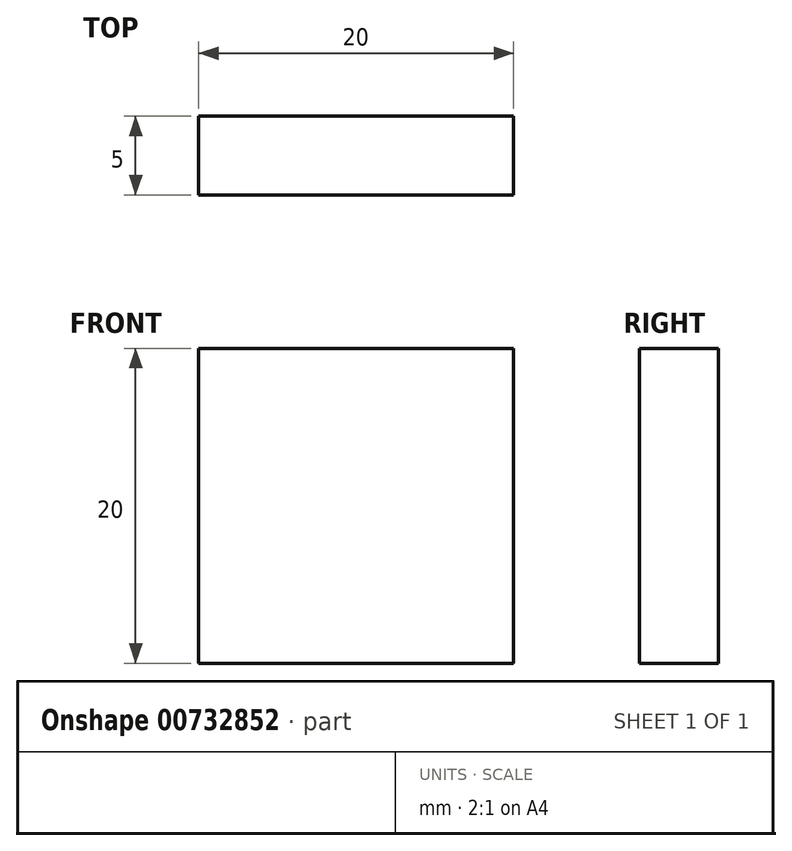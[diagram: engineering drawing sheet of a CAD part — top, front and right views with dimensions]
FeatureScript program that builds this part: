
annotation { "Feature Type Name" : "Feature", "Feature Type Description" : "" }
export const myFeature = defineFeature(function(context is Context, id is Id, definition is map)
    precondition{}
    {
        {
            var Q0;
            Q0=qCreatedBy(makeId("Front.planeOp"),FACE);
            var sketch = newSketch(context, id + "F0", { "sketchPlane" : qUnion([Q0])});
            skLineSegment(sketch, "E0.bottom", {"start": v(10, -10) * mm, "end": v(-10, -10) * mm});
            skLineSegment(sketch, "E0.top", {"start": v(10, 10) * mm, "end": v(-10, 10) * mm});
            skLineSegment(sketch, "E0.left", {"start": v(10, -10) * mm, "end": v(10, 10) * mm});
            skLineSegment(sketch, "E0.right", {"start": v(-10, -10) * mm, "end": v(-10, 10) * mm});
            skPoint(sketch, "E0.middle", {"position": v(0, 0) * mm});
            skSolve(sketch);
        }
        {
            var Q0;
            Q0=makeQuery(id+"F0.imprint","IMPRINT",FACE,{"disambiguationData":[TD([[makeQuery(id+"F0.imprint","IMPRINT",EDGE,{"derivedFrom":sQuery(id+"F0.wireOp",EDGE,"E0.bottom")}),-1.0]])]});
            extrude(context, id + "F1", {"entities" : qUnion([Q0]), "depth" : 5 * mm, "offsetDistance" : 25 * mm});
        }
    });
